# Revit family: Basin-Wallmount-Rectangle-DXV-Equility-D20175001
name_source: partatom
category: Plumbing Fixtures
revit_build: Autodesk Revit 2014 (Build: 20130308_1515(x64)
units: mm (PartAtom-declared; Revit-internal decimal feet)

## types (1)
- D20175001
    Assembly Code = D2010310
    CWFU = 1.5
    Default Elevation = 34"
    Description = Equility Wall-Hung Bathroom Sink
    Finish = Porcelain-DXV-Canvas White
    HWFU = 1.5
    Height = 7 1/16"
    Installation Type = Wall Mounted
    Length = 18"
    Manufacturer = DVX
    Material = Porcelain-DXV-Canvas White
    Model = D20175001
    Price = Prices may vary. Please consult Manufacturer Representative for most up-to-date price list.
    Product Documentation Link = https://dxv01.blob.core.windows.net
    Product Page URL = https://www.dxv.com
    URL = http://www.dxv.com
    Vent Connection = No
    WFU = 2
    Warranty Documentation Link = https://www.dxv.com
    Width = 22"

## geometry (parser evidence)
native form markers: Sweep x3
no freeform markers — native parametric forms only
